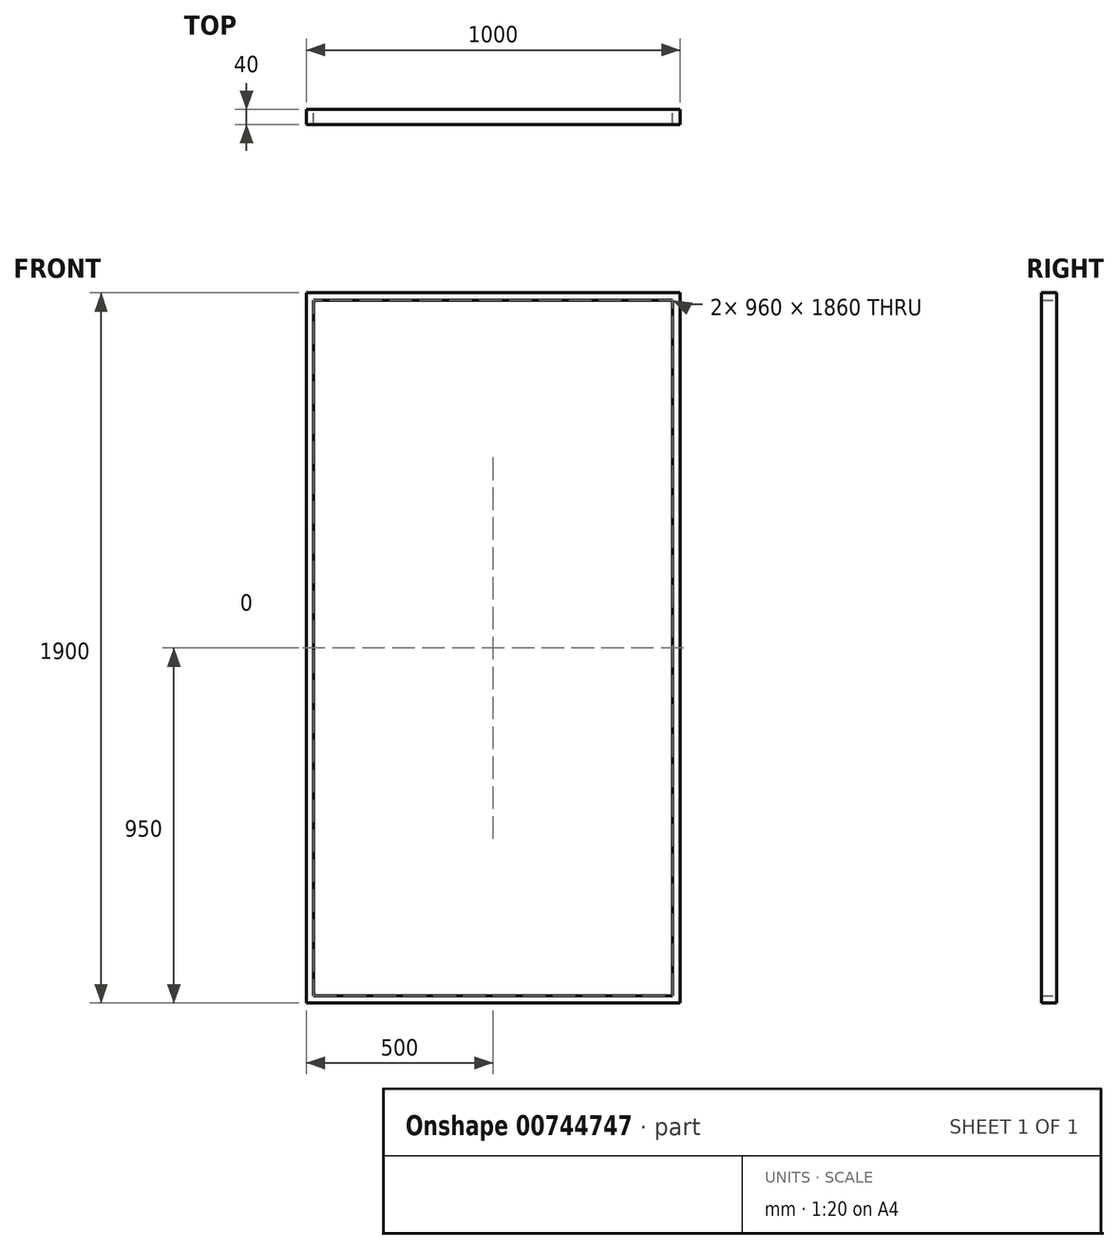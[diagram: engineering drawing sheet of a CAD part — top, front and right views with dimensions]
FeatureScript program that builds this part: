
annotation { "Feature Type Name" : "Feature", "Feature Type Description" : "" }
export const myFeature = defineFeature(function(context is Context, id is Id, definition is map)
    precondition{}
    {
        {
            var Q0;
            Q0=qCreatedBy(makeId("Front.planeOp"),FACE);
            var sketch = newSketch(context, id + "F0", { "sketchPlane" : qUnion([Q0])});
            skLineSegment(sketch, "E0.bottom", {"start": v(-500, 950) * mm, "end": v(500, 950) * mm});
            skLineSegment(sketch, "E0.top", {"start": v(-500, -950) * mm, "end": v(500, -950) * mm});
            skLineSegment(sketch, "E0.left", {"start": v(-500, 950) * mm, "end": v(-500, -950) * mm});
            skLineSegment(sketch, "E0.right", {"start": v(500, 950) * mm, "end": v(500, -950) * mm});
            skPoint(sketch, "E0.middle", {"position": v(0, 0) * mm});
            skLineSegment(sketch, "E1.0", {"start": v(-480, 930) * mm, "end": v(480, 930) * mm});
            skLineSegment(sketch, "E1.1", {"start": v(-480, 930) * mm, "end": v(-480, -930) * mm});
            skLineSegment(sketch, "E1.2", {"start": v(-480, -930) * mm, "end": v(480, -930) * mm});
            skLineSegment(sketch, "E1.3", {"start": v(480, 930) * mm, "end": v(480, -930) * mm});
            skSolve(sketch);
        }
        {
            var Q0;
            Q0=makeQuery(id+"F0.imprint","IMPRINT",FACE,{"disambiguationData":[TD([[makeQuery(id+"F0.imprint","IMPRINT",EDGE,{"derivedFrom":sQuery(id+"F0.wireOp",EDGE,"E0.bottom")}),-1.0]])]});
            extrude(context, id + "F1", {"entities" : qUnion([Q0]), "depth" : 40 * mm, "offsetDistance" : 25 * mm, "symmetric" : true});
        }
    });
